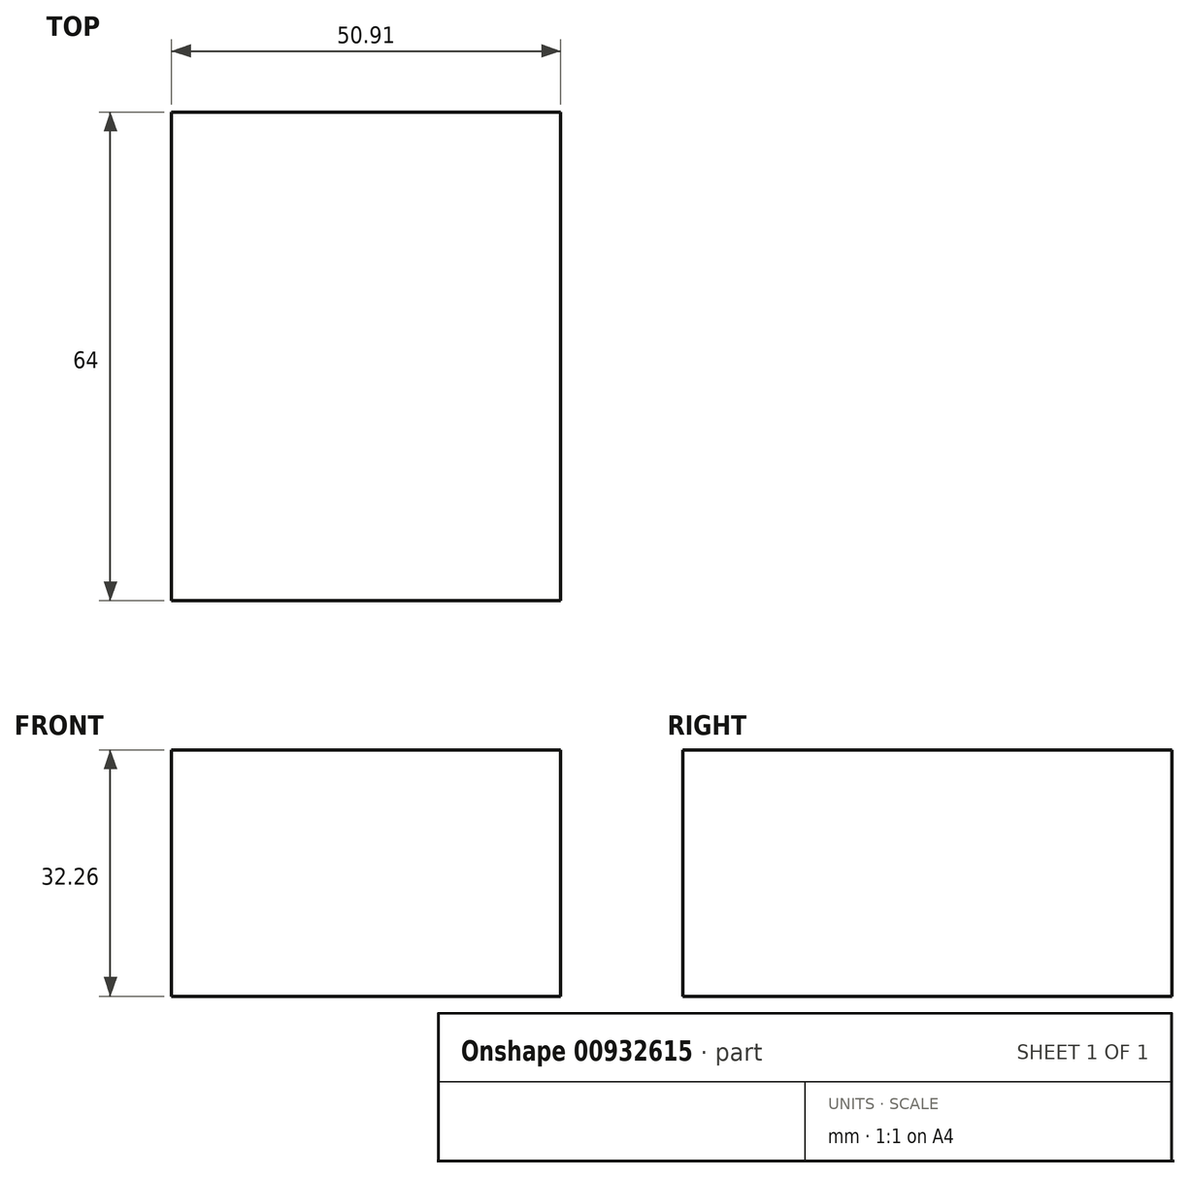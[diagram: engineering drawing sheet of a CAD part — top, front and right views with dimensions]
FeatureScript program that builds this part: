
annotation { "Feature Type Name" : "Feature", "Feature Type Description" : "" }
export const myFeature = defineFeature(function(context is Context, id is Id, definition is map)
    precondition{}
    {
        {
            var Q0;
            Q0=qCreatedBy(makeId("Front.planeOp"),FACE);
            var sketch = newSketch(context, id + "F0", { "sketchPlane" : qUnion([Q0])});
            skLineSegment(sketch, "E0.bottom", {"start": v(-82.8, 53.93) * mm, "end": v(-31.9, 53.93) * mm});
            skLineSegment(sketch, "E0.top", {"start": v(-82.8, 21.67) * mm, "end": v(-31.9, 21.67) * mm});
            skLineSegment(sketch, "E0.left", {"start": v(-82.8, 53.93) * mm, "end": v(-82.8, 21.67) * mm});
            skLineSegment(sketch, "E0.right", {"start": v(-31.9, 53.93) * mm, "end": v(-31.9, 21.67) * mm});
            skSolve(sketch);
        }
        {
            var Q0;
            Q0 = qSketchRegion(id + "F0", true);
            extrude(context, id + "F1", {"entities" : qUnion([Q0]), "depth" : 39 * mm, "offsetDistance" : 25 * mm});
        }
        {
            var Q0;
            Q0=makeQuery(id+"F1.opExtrude","CAP_FACE",FACE,{"disambiguationData":[OSD([sQuery(id+"F0.wireOp",EDGE,"E0.bottom"),sQuery(id+"F0.wireOp",EDGE,"E0.top"),sQuery(id+"F0.wireOp",EDGE,"E0.left"),sQuery(id+"F0.wireOp",EDGE,"E0.right")])],"isStart":true});
            extrude(context, id + "F2", {"entities" : qUnion([Q0]), "operationType" : NewBodyOperationType.ADD, "depth" : 25 * mm, "offsetDistance" : 25 * mm});
        }
    });
